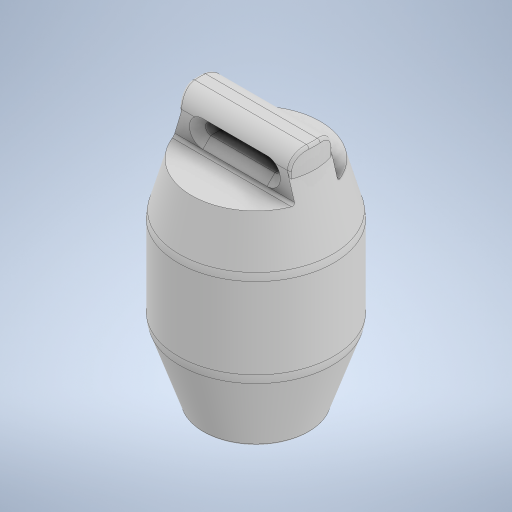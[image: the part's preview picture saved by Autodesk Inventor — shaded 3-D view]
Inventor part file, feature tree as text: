
AUTODESK INVENTOR PART (.ipt)
format: ipt  version: 2023.4 (Build 274418000, 418)  size: 454,144 bytes
history: native  units: mm
features: fillet x5, chamfer x4, sketch x4, extrude x3, revolve x1
ambient origin geometry x8: Origin, YZ Plane, XZ Plane, XY Plane, X Axis, Y Axis, Z Axis, Center Point
bodies: Solid1 (feature_tree)
feature tree (17):
  revolve  "Revolution1"  [1 undecoded]
  extrude  "Extrusion1"  TaperAngle=0.0deg  [1 undecoded]
  extrude  "Extrusion2"  Depth=2.0mm
  fillet  "Fillet1"  Radius=16.0mm
  chamfer  "Chamfer1"  Distance=16.0mm
  fillet  "Fillet2"  Radius=8.0mm
  fillet  "Fillet3"  Radius=22.0mm
  fillet  "Fillet4"  [1 undecoded]
  chamfer  "Chamfer2"  Distance=8.0mm
  extrude  "Extrusion3"  Depth=10.0mm
  chamfer  "Chamfer3"  Distance=16.0mm
  fillet  "Fillet5"  Radius=28.0mm
  chamfer  "Chamfer4"  Distance=4.0mm
  sketch  "Sketch1"  dims[d0=7.05mm d2=0.0mm]
  sketch  "Sketch2"  dims[d3=14.0mm d4=0.0mm]
  sketch  "Sketch3"  dims[d6=8.05mm d7=2.0mm d8=16.0mm]
  sketch  "Sketch4"  dims[d9=28.0mm d10=16.0mm d11=8.0mm d12=22.0mm d13=360.0deg d14=8.0mm d15=8.0mm d16=16.0mm d17=0.0mm d18=28.0mm d19=4.0mm d20=8.0mm d21=0.0mm d22=0.0mm d23=2.0mm d24=3.0mm d25=2.0mm d26=45.0deg d27=6.0mm d28=1.0mm d29=10.0mm d30=1.0mm d31=2.0mm d32=45.0deg d33=30.6mm d34=0.0mm d35=0.5mm d36=4.0mm d37=2.0mm d38=45.0deg d39=1.0mm d40=0.5mm d41=2.0mm d42=45.0deg d43=28.0mm d44=41.2mm]
note: 3 required parameter values undecoded (feature->parameter linkage not recoverable at this tier; creation-order binding heuristic only, values carry confidence <= 0.55)